# Revit family: NeorestRS_P_TAC
name_source: partatom
category: Plumbing Fixtures
revit_build: Autodesk Revit 2018 (Build: 20170223_1515(x64)
units: mm (PartAtom-declared; Revit-internal decimal feet)

## family parameters
Always vertical = Yes
Cut with Voids When Loaded = No
OmniClass Number = 23.45.00.00
OmniClass Title = Sanitary, Laundry, and Cleaning Equipment
Part Type = Normal
Room Calculation Point = No
Round Connector Dimension = Use Diameter
Shared = No
Work Plane-Based = No

## types (1)
- NeorestRS_P_TAC
    CW Connection = Yes
    Description = SMART TOILET NEOREST RS
    Finish = White
    HW Connection = No
    Height = 515 mm  [stored 1.68963 ft]
    Length = 690 mm  [stored 2.26378 ft]
    Manufacturer = TOTO LTD.
    Material = Ceramic
    Model = "Bowl Unit
CS921P VT
Top Unit
TCF83410GAA（Remotecontroller:White）"
    Seat Included = Yes
    URL = https://asia.toto.com
    Vent Connection = No
    Voltage = 220-240V
    Waste Connection = Yes
    Water Pressure = 0.05MPa～0.75MPa
    Water Use = 4.5L/3.0L
    Width = 386 mm  [stored 1.2664 ft]

note: [stored X ft] marks values corroborated as IEEE doubles in the binary element streams (Revit-internal decimal feet)

## geometry (parser evidence)
native form markers: Sweep x2
no freeform markers — native parametric forms only
